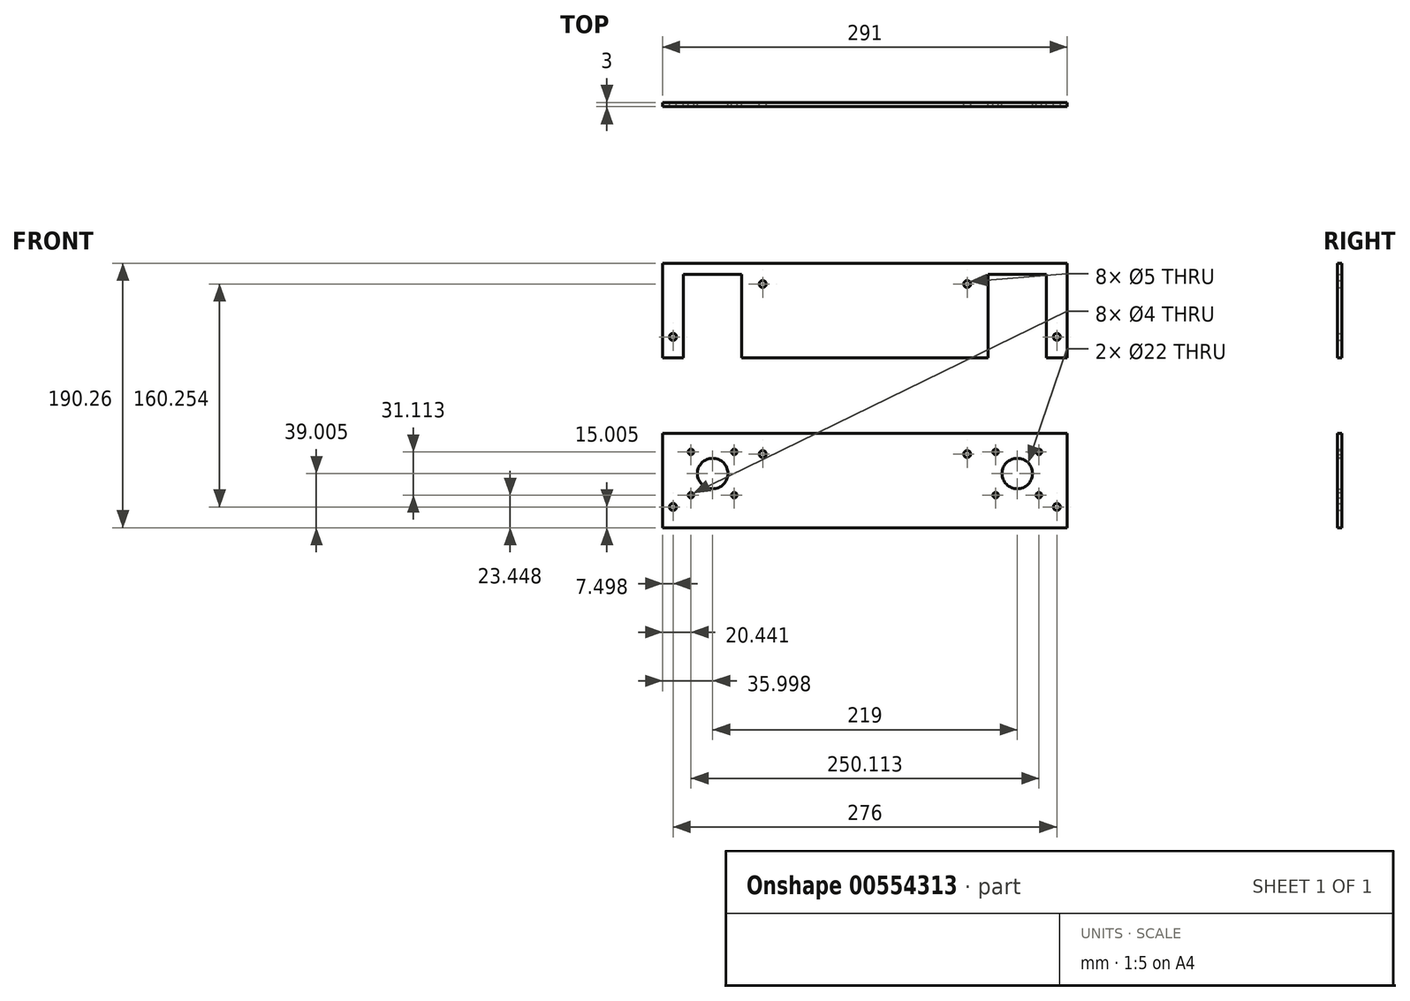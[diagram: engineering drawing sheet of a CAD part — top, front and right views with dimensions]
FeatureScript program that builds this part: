
annotation { "Feature Type Name" : "Feature", "Feature Type Description" : "" }
export const myFeature = defineFeature(function(context is Context, id is Id, definition is map)
    precondition{}
    {
        {
            var Q0;
            Q0=qCreatedBy(makeId("Front.planeOp"),FACE);
            var sketch = newSketch(context, id + "F0", { "sketchPlane" : qUnion([Q0])});
            skLineSegment(sketch, "E0.bottom", {"start": v(-243.44, 89.97) * mm, "end": v(47.56, 89.97) * mm});
            skLineSegment(sketch, "E0.top", {"start": v(-243.44, 21.97) * mm, "end": v(-228.44, 21.97) * mm});
            skLineSegment(sketch, "E0.left", {"start": v(-243.44, 89.97) * mm, "end": v(-243.44, 21.97) * mm});
            skLineSegment(sketch, "E0.right", {"start": v(47.56, 89.97) * mm, "end": v(47.56, 21.97) * mm});
            skLineSegment(sketch, "E1.bottom", {"start": v(-243.44, -32.29) * mm, "end": v(47.56, -32.29) * mm});
            skLineSegment(sketch, "E1.top", {"start": v(-243.44, -100.29) * mm, "end": v(47.56, -100.29) * mm});
            skLineSegment(sketch, "E1.left", {"start": v(-243.44, -32.29) * mm, "end": v(-243.44, -100.29) * mm});
            skLineSegment(sketch, "E1.right", {"start": v(47.56, -32.29) * mm, "end": v(47.56, -100.29) * mm});
            skLineSegment(sketch, "E2", {"start": v(32.56, 21.97) * mm, "end": v(32.56, 81.97) * mm});
            skLineSegment(sketch, "E3", {"start": v(32.56, 81.97) * mm, "end": v(-9.44, 81.97) * mm});
            skLineSegment(sketch, "E4", {"start": v(-9.44, 81.97) * mm, "end": v(-9.44, 21.97) * mm});
            skLineSegment(sketch, "E5", {"start": v(32.56, -82.29) * mm, "end": v(32.56, -40.29) * mm, "construction": true});
            skLineSegment(sketch, "E6", {"start": v(32.56, -40.29) * mm, "end": v(-9.44, -40.29) * mm, "construction": true});
            skLineSegment(sketch, "E7", {"start": v(-9.44, -40.29) * mm, "end": v(-9.44, -82.29) * mm, "construction": true});
            skLineSegment(sketch, "E8", {"start": v(-228.44, -82.29) * mm, "end": v(-228.44, -40.29) * mm, "construction": true});
            skLineSegment(sketch, "E9", {"start": v(-228.44, -40.29) * mm, "end": v(-186.44, -40.29) * mm, "construction": true});
            skLineSegment(sketch, "E10", {"start": v(-186.44, -40.29) * mm, "end": v(-186.44, -82.29) * mm, "construction": true});
            skLineSegment(sketch, "E11", {"start": v(-228.44, 21.97) * mm, "end": v(-228.44, 81.97) * mm});
            skLineSegment(sketch, "E12", {"start": v(-228.44, 81.97) * mm, "end": v(-186.44, 81.97) * mm});
            skLineSegment(sketch, "E13", {"start": v(-186.44, 81.97) * mm, "end": v(-186.44, 21.97) * mm});
            skLineSegment(sketch, "E14", {"start": v(-228.44, -82.29) * mm, "end": v(-186.44, -82.29) * mm, "construction": true});
            skLineSegment(sketch, "E15", {"start": v(-9.44, -82.29) * mm, "end": v(32.56, -82.29) * mm, "construction": true});
            skCircle(sketch, "E16", {"center": v(-235.94, 36.97) * mm, "radius": 2.5 * mm});
            skCircle(sketch, "E17", {"center": v(-171.44, 74.97) * mm, "radius": 2.5 * mm});
            skCircle(sketch, "E18", {"center": v(-24.44, 74.97) * mm, "radius": 2.5 * mm});
            skCircle(sketch, "E19", {"center": v(40.06, 36.97) * mm, "radius": 2.5 * mm});
            skLineSegment(sketch, "E20.trimOffspring", {"start": v(-186.44, 21.97) * mm, "end": v(-9.44, 21.97) * mm});
            skLineSegment(sketch, "E21.trimOffspring", {"start": v(32.56, 21.97) * mm, "end": v(47.56, 21.97) * mm});
            skLineSegment(sketch, "E22", {"start": v(-228.44, -40.29) * mm, "end": v(-186.44, -82.29) * mm, "construction": true});
            skLineSegment(sketch, "E23", {"start": v(-228.44, -82.29) * mm, "end": v(-186.44, -40.29) * mm, "construction": true});
            skLineSegment(sketch, "E24", {"start": v(-9.44, -40.29) * mm, "end": v(32.56, -82.29) * mm, "construction": true});
            skLineSegment(sketch, "E25", {"start": v(-9.44, -82.29) * mm, "end": v(32.56, -40.29) * mm, "construction": true});
            skCircle(sketch, "E26", {"center": v(-207.44, -61.29) * mm, "radius": 11 * mm});
            skCircle(sketch, "E27", {"center": v(11.56, -61.29) * mm, "radius": 11 * mm});
            skCircle(sketch, "E28", {"center": v(-235.94, -85.29) * mm, "radius": 2.5 * mm});
            skCircle(sketch, "E29", {"center": v(-171.44, -47.29) * mm, "radius": 2.5 * mm});
            skCircle(sketch, "E30", {"center": v(-24.44, -47.29) * mm, "radius": 2.5 * mm});
            skCircle(sketch, "E31", {"center": v(40.06, -85.29) * mm, "radius": 2.5 * mm});
            skCircle(sketch, "E32", {"center": v(-223, -45.73) * mm, "radius": 2 * mm});
            skCircle(sketch, "E33.1.0", {"center": v(-223, -76.84) * mm, "radius": 2 * mm});
            skCircle(sketch, "E33.2.0", {"center": v(-191.89, -76.84) * mm, "radius": 2 * mm});
            skCircle(sketch, "E33.3.0", {"center": v(-191.89, -45.73) * mm, "radius": 2 * mm});
            skCircle(sketch, "E34", {"center": v(27.11, -45.73) * mm, "radius": 2 * mm});
            skCircle(sketch, "E35.1.0", {"center": v(-4, -45.73) * mm, "radius": 2 * mm});
            skCircle(sketch, "E35.2.0", {"center": v(-4, -76.84) * mm, "radius": 2 * mm});
            skCircle(sketch, "E35.3.0", {"center": v(27.11, -76.84) * mm, "radius": 2 * mm});
            skSolve(sketch);
        }
        {
            var Q0;
            Q0 = qSketchRegion(id + "F0", true);
            extrude(context, id + "F1", {"entities" : qUnion([Q0]), "depth" : 3 * mm, "offsetDistance" : 25 * mm});
        }
    });
